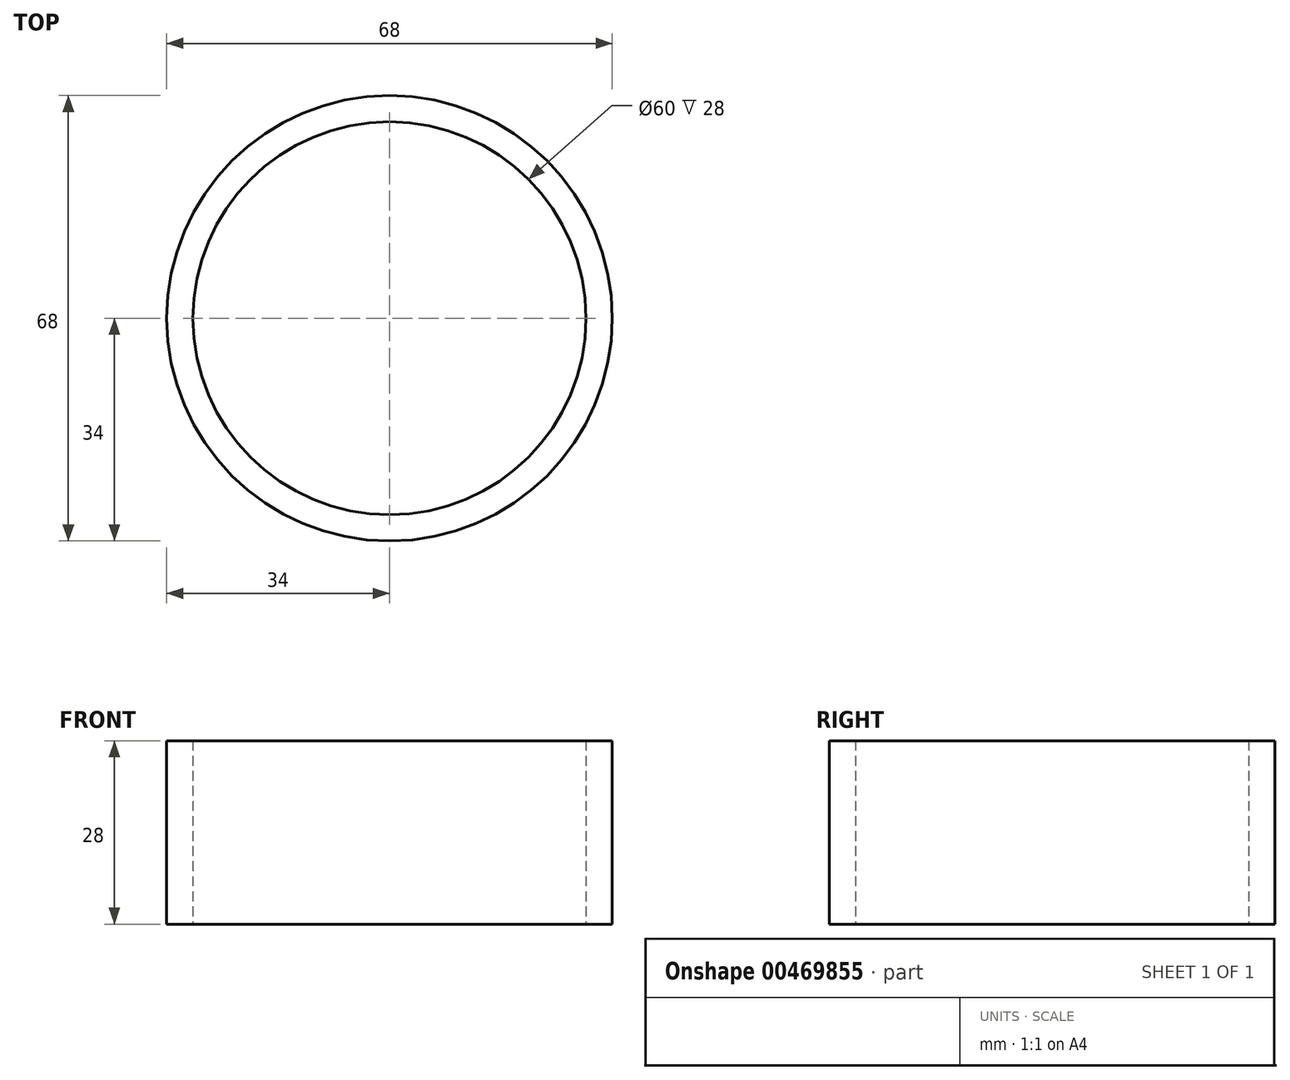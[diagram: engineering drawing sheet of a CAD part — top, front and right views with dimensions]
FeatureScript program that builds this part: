
annotation { "Feature Type Name" : "Feature", "Feature Type Description" : "" }
export const myFeature = defineFeature(function(context is Context, id is Id, definition is map)
    precondition{}
    {
        {
            var Q0;
            Q0=qCreatedBy(makeId("Top.planeOp"),FACE);
            var sketch = newSketch(context, id + "F0", { "sketchPlane" : qUnion([Q0])});
            skCircle(sketch, "E0", {"center": v(0, 0) * mm, "radius": 30 * mm});
            skCircle(sketch, "E1", {"center": v(0, 0) * mm, "radius": 34 * mm});
            skSolve(sketch);
        }
        {
            var Q0;
            Q0 = qSketchRegion(id + "F0", true);
            extrude(context, id + "F1", {"entities" : qUnion([Q0]), "depth" : 28 * mm});
        }
    });
